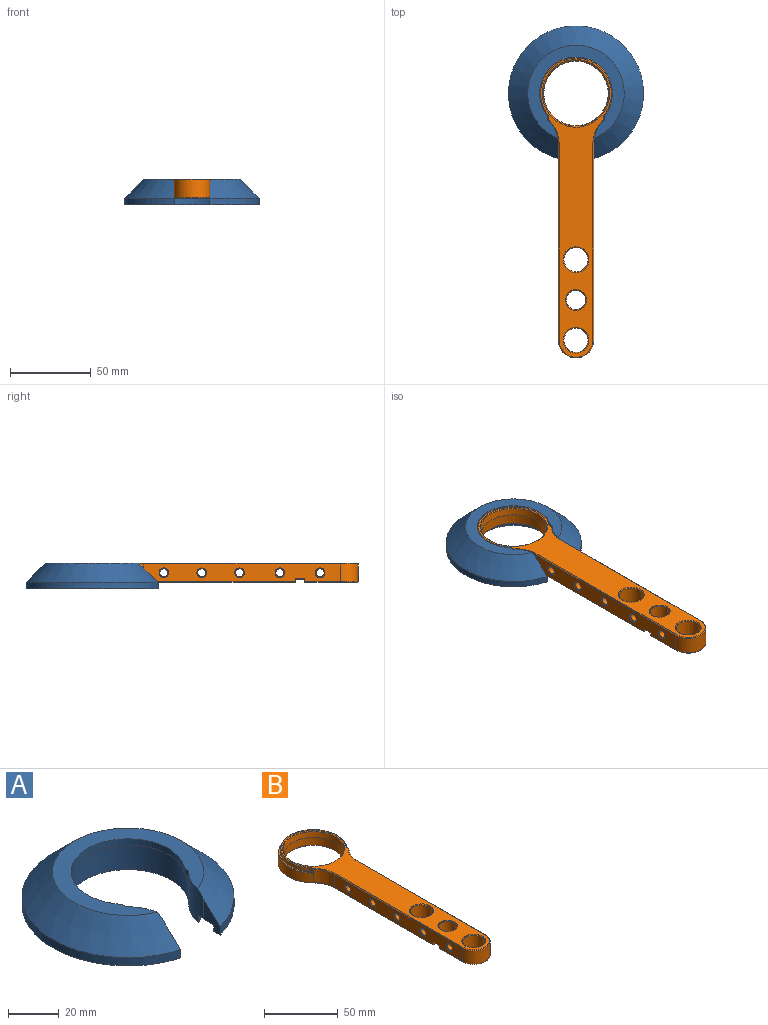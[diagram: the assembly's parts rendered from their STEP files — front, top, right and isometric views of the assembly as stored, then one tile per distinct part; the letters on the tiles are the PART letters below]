
ASSEMBLY  parts=2 mates=1
PART A: 75 faces, bbox 84.2x82.8x16.3 mm
  f0: cylinder r=19.95mm len=16mm, axis (0,0,-1), area 229.2mm2, adj f2,f36,f42,f43,f46,f51,f52,f72
  f1: cylinder r=19.95mm len=16mm, axis (0,0,-1), area 229.2mm2, adj f2,f35,f42,f43,f47,f51,f53,f69
  f2: plane 58.74x53.48mm, normal (0,0,-1), area 238.1mm2, adj f0,f1,f3,f4,f5,f6,f7,f8
  f3: cylinder r=18.5mm len=14.5mm, axis (0,0,-1), area 189mm2, adj f2,f38,f39,f49,f50,f72,f74
  f4: cylinder r=18.5mm len=14.5mm, axis (0,0,-1), area 189mm2, adj f2,f24,f25,f26,f48,f69,f70
  f5: plane 14.99x14.54mm, normal (1,0,0), area 129.4mm2, adj f2,f15,f16,f17,f18,f45,f66,f67
  f6: plane 14.99x14.54mm, normal (-1,0,0), area 129.4mm2, adj f2,f31,f32,f33,f34,f45,f66,f67
  f7: plane 14.54x12.99mm, normal (0.5,0.87,0), area 129.4mm2, adj f2,f31,f32,f33,f34,f45,f63,f64
  f8: plane 14.54x12.99mm, normal (-0.5,-0.87,0), area 129.4mm2, adj f2,f27,f28,f29,f30,f45,f63,f64
  f9: plane 14.54x12.99mm, normal (-0.5,0.87,0), area 129.4mm2, adj f2,f27,f28,f29,f30,f45,f60,f61
  f10: plane 14.54x12.99mm, normal (0.5,-0.87,0), area 129.4mm2, adj f2,f23,f24,f25,f26,f45,f60,f61
  f11: plane 14.54x12.99mm, normal (-0.5,-0.87,0), area 129.4mm2, adj f2,f37,f38,f39,f45,f50,f57,f58
  f12: plane 14.54x12.99mm, normal (0.5,0.87,0), area 129.4mm2, adj f2,f19,f20,f21,f22,f45,f57,f58
  f13: plane 14.54x12.99mm, normal (0.5,-0.87,0), area 129.4mm2, adj f2,f19,f20,f21,f22,f45,f54,f55
  f14: plane 14.54x12.99mm, normal (-0.5,0.87,0), area 129.4mm2, adj f2,f15,f16,f17,f18,f45,f54,f55
  f15: cylinder r=40.45mm len=33.9mm, axis (0,0,-1), area 138mm2, adj f5,f14,f16,f45
  f16: cone r=40.45mm half-angle=45deg, axis (0,0,-1), area 550.6mm2, adj f5,f14,f15,f17
  f17: plane 24.27x15.93mm, normal (0,0,-1), area 104.2mm2, adj f5,f14,f16,f18
  f18: cylinder r=25.5mm len=20.95mm, axis (0,0,-1), area 365.4mm2, adj f2,f5,f14,f17
  f19: cylinder r=40.45mm len=39.14mm, axis (0,0,-1), area 138mm2, adj f12,f13,f20,f45
  f20: cone r=40.45mm half-angle=45deg, axis (0,0,-1), area 550.6mm2, adj f12,f13,f19,f21
  f21: plane 28.02x6.88mm, normal (0,0,-1), area 104.2mm2, adj f12,f13,f20,f22
  f22: cylinder r=25.5mm len=24.19mm, axis (0,0,-1), area 365.4mm2, adj f2,f12,f13,f21
  f23: cylinder r=40.45mm len=22.15mm, axis (0,0,-1), area 97.6mm2, adj f10,f24,f45,f48
  f24: cone r=40.45mm half-angle=45deg, axis (0,0,-1), area 357.9mm2, adj f4,f10,f23,f25,f48
  f25: plane 12.8x11.82mm, normal (0,0,-1), area 48.4mm2, adj f4,f10,f24,f26
  f26: cylinder r=25.5mm len=14.5mm, axis (0,0,-1), area 87.3mm2, adj f2,f4,f10,f25
  f27: cylinder r=40.45mm len=39.14mm, axis (0,0,-1), area 138mm2, adj f8,f9,f28,f45
  f28: cone r=40.45mm half-angle=45deg, axis (0,0,-1), area 550.6mm2, adj f8,f9,f27,f29
  f29: plane 28.02x6.88mm, normal (0,0,-1), area 104.2mm2, adj f8,f9,f28,f30
  f30: cylinder r=25.5mm len=24.19mm, axis (0,0,-1), area 365.4mm2, adj f2,f8,f9,f29
  f31: cylinder r=40.45mm len=33.9mm, axis (0,0,-1), area 138mm2, adj f6,f7,f32,f45
  f32: cone r=40.45mm half-angle=45deg, axis (0,0,-1), area 550.6mm2, adj f6,f7,f31,f33
  f33: plane 24.27x15.93mm, normal (0,0,-1), area 104.2mm2, adj f6,f7,f32,f34
  f34: cylinder r=25.5mm len=20.95mm, axis (0,0,-1), area 365.4mm2, adj f2,f6,f7,f33
  f35: cylinder r=3.95mm len=3.19mm, axis (0,0,-1), area 10.1mm2, adj f1,f40,f41,f42
  f36: cylinder r=3.95mm len=3.19mm, axis (0,0,-1), area 10.1mm2, adj f0,f40,f41,f42
  f37: cylinder r=40.45mm len=22.15mm, axis (0,0,-1), area 97.6mm2, adj f11,f38,f45,f49
  f38: cone r=40.45mm half-angle=45deg, axis (0,0,-1), area 357.9mm2, adj f3,f11,f37,f39,f49
  f39: plane 12.8x11.82mm, normal (0,0,-1), area 48.4mm2, adj f3,f11,f38,f50
  f40: plane 48.15x40.62mm, normal (0,0,-1), area 163.2mm2, adj f35,f36,f41,f51
  f41: cylinder r=22.55mm len=45.1mm, axis (0,0,-1), area 298.3mm2, adj f35,f36,f40,f42
  f42: plane 59.9x57.66mm, normal (0,0,1), area 1003.5mm2, adj f0,f1,f35,f36,f41,f43
  f43: cone r=41.95mm half-angle=45deg, axis (0,0,-1), area 3447.3mm2, adj f0,f1,f42,f44,f46,f47
  f44: cylinder r=41.95mm len=83.9mm, axis (0,0,-1), area 964.9mm2, adj f43,f45,f46,f47
  f45: plane 83.9x82.42mm, normal (0,0,-1), area 375.8mm2, adj f5,f6,f7,f8,f9,f10,f11,f12
  f46: plane 13.16x9.58mm, normal (-1,0,0), area 60mm2, adj f0,f43,f44,f45,f73,f74
  f47: plane 13.16x9.58mm, normal (1,0,0), area 60mm2, adj f1,f43,f44,f45,f69,f71
  f48: plane 10.43x7.48mm, normal (-1,0,0), area 32.8mm2, adj f4,f23,f24,f45,f69,f71
  f49: plane 10.43x7.48mm, normal (1,0,0), area 32.8mm2, adj f3,f37,f38,f45,f73,f74
  f50: cylinder r=25.5mm len=14.5mm, axis (0,0,-1), area 87.3mm2, adj f2,f3,f11,f39
  f51: cylinder r=24.08mm len=48.15mm, axis (0,0,-1), area 1497mm2, adj f0,f1,f2,f40,f52,f53
  f52: plane 1.08x1.07mm, normal (0,0,-1), area 0mm2, adj f0,f51
  f53: plane 1.08x1.07mm, normal (0,0,-1), area 0mm2, adj f1,f51
  f54: plane 7.68x5.3mm, normal (0,0,-1), area 12mm2, adj f13,f14,f55,f56
  f55: cylinder r=38.45mm len=3.2mm, axis (0,0,-1), area 4.8mm2, adj f13,f14,f45,f54
  f56: cylinder r=30.45mm len=3.2mm, axis (0,0,-1), area 4.8mm2, adj f2,f13,f14,f54
  f57: plane 7.68x5.3mm, normal (0,0,-1), area 12mm2, adj f11,f12,f58,f59
  f58: cylinder r=38.45mm len=3.2mm, axis (0,0,-1), area 4.8mm2, adj f11,f12,f45,f57
  f59: cylinder r=30.45mm len=3.2mm, axis (0,0,-1), area 4.8mm2, adj f2,f11,f12,f57
  f60: plane 7.68x5.3mm, normal (0,0,-1), area 12mm2, adj f9,f10,f61,f62
  f61: cylinder r=38.45mm len=3.2mm, axis (0,0,-1), area 4.8mm2, adj f9,f10,f45,f60
  f62: cylinder r=30.45mm len=3.2mm, axis (0,0,-1), area 4.8mm2, adj f2,f9,f10,f60
  f63: plane 7.68x5.3mm, normal (0,0,-1), area 12mm2, adj f7,f8,f64,f65
  f64: cylinder r=38.45mm len=3.2mm, axis (0,0,-1), area 4.8mm2, adj f7,f8,f45,f63
  f65: cylinder r=30.45mm len=3.2mm, axis (0,0,-1), area 4.8mm2, adj f2,f7,f8,f63
  f66: plane 8.01x1.5mm, normal (0,0,-1), area 12mm2, adj f5,f6,f67,f68
  f67: cylinder r=38.45mm len=3.2mm, axis (0,0,-1), area 4.8mm2, adj f5,f6,f45,f66
  f68: cylinder r=30.45mm len=3.2mm, axis (0,0,-1), area 4.8mm2, adj f2,f5,f6,f66
  f69: plane 9.23x1.81mm, normal (0,0,-1), area 12.6mm2, adj f1,f4,f47,f48,f70,f71
  f70: cylinder r=30.45mm len=3.2mm, axis (0,0,-1), area 5.5mm2, adj f1,f2,f4,f69
  f71: cylinder r=38.45mm len=3.2mm, axis (0,0,-1), area 4.9mm2, adj f45,f47,f48,f69
  f72: cylinder r=30.45mm len=3.2mm, axis (0,0,-1), area 5.5mm2, adj f0,f2,f3,f74
  f73: cylinder r=38.45mm len=3.2mm, axis (0,0,-1), area 4.9mm2, adj f45,f46,f49,f74
  f74: plane 9.23x1.81mm, normal (0,0,-1), area 12.6mm2, adj f0,f3,f46,f49,f72,f73
PART B: 91 faces, bbox 48x188.2x12 mm
  f0: cylinder r=24mm len=48mm, axis (0,0,-1), area 910.7mm2, adj f5,f11,f26,f27,f35,f42,f43,f62
  f1: plane 185.73x44mm, normal (0,0,1), area 2605.8mm2, adj f33,f34,f35,f36,f37,f38,f39,f40
  f2: plane 148.73x47mm, normal (0,0,-1), area 2328.4mm2, adj f54,f55,f58,f59,f62,f63,f65,f66
  f3: cylinder r=8mm len=14.29mm, axis (0,0,-1), area 26.5mm2, adj f15,f31,f32,f52
  f4: cylinder r=6mm len=12mm, axis (0,0,-1), area 320.4mm2, adj f44,f90
  f5: cylinder r=20mm len=14.19mm, axis (0,0,-1), area 173.6mm2, adj f0,f6,f33,f58
  f6: plane 122x11mm, normal (-1,0,0), area 1188.6mm2, adj f5,f7,f34,f45,f47,f48,f53,f54
  f7: cylinder r=11mm len=22mm, axis (0,0,-1), area 380.1mm2, adj f6,f8,f36,f57
  f8: plane 122x11mm, normal (1,0,0), area 1188.6mm2, adj f7,f11,f38,f61,f67,f68,f70,f72
  f9: cylinder r=7.5mm len=15mm, axis (0,0,-1), area 518.4mm2, adj f74,f85
  f10: cylinder r=7.5mm len=15mm, axis (0,0,-1), area 518.4mm2, adj f73,f87
  f11: cylinder r=20mm len=14.19mm, axis (0,0,-1), area 173.6mm2, adj f0,f8,f40,f65
  f12: cylinder r=20mm len=40mm, axis (0,0,-1), area 816.8mm2, adj f86,f88
  f13: plane 32.5x21mm, normal (0,0,-1), area 370.2mm2, adj f46,f49,f52,f53,f56,f57,f60,f61
  f14: cylinder r=8mm len=14.29mm, axis (0,0,-1), area 26.5mm2, adj f15,f29,f30,f63
  f15: plane 21x16mm, normal (0,0,-1), area 74.6mm2, adj f3,f14,f21,f22,f23,f24,f29,f30
  f16: cylinder r=2.5mm len=21mm, axis (1,0,0), area 329.9mm2, adj f75,f76
  f17: cylinder r=2.5mm len=21mm, axis (1,0,0), area 329.9mm2, adj f77,f78
  f18: cylinder r=2.5mm len=21mm, axis (1,0,0), area 329.9mm2, adj f79,f80
  f19: cylinder r=2.5mm len=21mm, axis (1,0,0), area 329.9mm2, adj f81,f82
  f20: cylinder r=2.5mm len=21mm, axis (1,0,0), area 329.9mm2, adj f83,f84
  f21: plane 1.57x1.5mm, normal (0,-1,0), area 2.4mm2, adj f15,f30,f48,f55
  f22: plane 1.57x1.5mm, normal (0,1,0), area 2.4mm2, adj f15,f32,f46,f47
  f23: plane 1.57x1.5mm, normal (0,-1,0), area 2.4mm2, adj f15,f29,f69,f72
  f24: plane 1.57x1.5mm, normal (0,1,0), area 2.4mm2, adj f15,f31,f60,f67
  f25: plane 47x39.35mm, normal (0,0,1), area 104.8mm2, adj f26,f27,f28,f43
  f26: cylinder r=4mm len=3.17mm, axis (0,0,1), area 8.5mm2, adj f0,f25,f28,f37,f43
  f27: cylinder r=4mm len=3.17mm, axis (0,0,1), area 8.5mm2, adj f0,f25,f28,f41,f43
  f28: cylinder r=22.5mm len=45mm, axis (0,0,1), area 248mm2, adj f25,f26,f27,f39
  f29: cylinder r=2mm len=1.79mm, axis (0,0,-1), area 3.3mm2, adj f14,f15,f23,f66
  f30: cylinder r=2mm len=1.79mm, axis (0,0,-1), area 3.3mm2, adj f14,f15,f21,f59
  f31: cylinder r=2mm len=1.79mm, axis (0,0,-1), area 3.3mm2, adj f3,f15,f24,f56
  f32: cylinder r=2mm len=1.79mm, axis (0,0,-1), area 3.3mm2, adj f3,f15,f22,f49
  f33: cone r=20mm half-angle=45deg, axis (0,0,1), area 11.3mm2, adj f1,f5,f34,f35
  f34: plane 122x0.5mm, normal (-0.71,0,0.71), area 86.3mm2, adj f1,f6,f33,f36
  f35: cone r=23.5mm half-angle=45deg, axis (0,0,-1), area 0.4mm2, adj f0,f1,f33,f37
  f36: cone r=10.5mm half-angle=45deg, axis (0,0,-1), area 23.9mm2, adj f1,f7,f34,f38
  f37: cone r=4.5mm half-angle=45deg, axis (0,0,1), area 2.4mm2, adj f1,f26,f35,f39
  f38: plane 122x0.5mm, normal (0.71,0,0.71), area 86.3mm2, adj f1,f8,f36,f40
  f39: cone r=22mm half-angle=45deg, axis (0,0,-1), area 69.4mm2, adj f1,f28,f37,f41
  f40: cone r=20mm half-angle=45deg, axis (0,0,1), area 11.3mm2, adj f1,f11,f38,f42
  f41: cone r=4mm half-angle=45deg, axis (0,0,1), area 2.4mm2, adj f1,f27,f39,f42
  f42: cone r=23.5mm half-angle=45deg, axis (0,0,-1), area 0.4mm2, adj f0,f1,f40,f41
  f43: cone r=23.5mm half-angle=45deg, axis (0,0,-1), area 77.9mm2, adj f0,f25,f26,f27
  f44: cone r=6mm half-angle=45deg, axis (0,0,1), area 27.8mm2, adj f1,f4
  f45: plane 6x0.5mm, normal (-0.71,0,-0.71), area 3.9mm2, adj f6,f15,f47,f48
  f46: plane 1.57x0.5mm, normal (0,0.71,-0.71), area 1.1mm2, adj f13,f22,f49,f50
  f47: plane 2x0.5mm, normal (-0.71,0.71,0), area 1.2mm2, adj f6,f22,f45,f50
  f48: plane 2x0.5mm, normal (-0.71,-0.71,0), area 1.2mm2, adj f6,f21,f45,f51
  f49: cone r=1.5mm half-angle=45deg, axis (0,0,1), area 1.4mm2, adj f13,f32,f46,f52
  f50: plane 0.5x0.5mm, normal (-0.58,0.58,-0.58), area 0.2mm2, adj f46,f47,f53
  f51: plane 0.5x0.5mm, normal (-0.58,-0.58,-0.58), area 0.2mm2, adj f48,f54,f55
  f52: cone r=8mm half-angle=45deg, axis (0,0,-1), area 12.9mm2, adj f3,f13,f49,f56
  f53: plane 22x0.5mm, normal (-0.71,0,-0.71), area 15.6mm2, adj f6,f13,f50,f57
  f54: plane 94x0.5mm, normal (-0.71,0,-0.71), area 66.5mm2, adj f2,f6,f51,f58
  f55: plane 1.57x0.5mm, normal (0,-0.71,-0.71), area 1.1mm2, adj f2,f21,f51,f59
  f56: cone r=1.5mm half-angle=45deg, axis (0,0,1), area 1.4mm2, adj f13,f31,f52,f60
  f57: cone r=11mm half-angle=45deg, axis (0,0,1), area 23.9mm2, adj f7,f13,f53,f61
  f58: cone r=20.5mm half-angle=45deg, axis (0,0,-1), area 11.3mm2, adj f2,f5,f54,f62
  f59: cone r=1.5mm half-angle=45deg, axis (0,0,1), area 1.4mm2, adj f2,f30,f55,f63
  f60: plane 1.57x0.5mm, normal (0,0.71,-0.71), area 1.1mm2, adj f13,f24,f56,f64
  f61: plane 22x0.5mm, normal (0.71,0,-0.71), area 15.6mm2, adj f8,f13,f57,f64
  f62: cone r=24mm half-angle=45deg, axis (0,0,1), area 79.3mm2, adj f0,f2,f58,f65
  f63: cone r=8mm half-angle=45deg, axis (0,0,-1), area 12.9mm2, adj f2,f14,f59,f66
  f64: plane 0.5x0.5mm, normal (0.58,0.58,-0.58), area 0.2mm2, adj f60,f61,f67
  f65: cone r=20.5mm half-angle=45deg, axis (0,0,-1), area 11.3mm2, adj f2,f11,f62,f68
  f66: cone r=1.5mm half-angle=45deg, axis (0,0,1), area 1.4mm2, adj f2,f29,f63,f69
  f67: plane 2x0.5mm, normal (0.71,0.71,0), area 1.2mm2, adj f8,f24,f64,f70
  f68: plane 94x0.5mm, normal (0.71,0,-0.71), area 66.5mm2, adj f2,f8,f65,f71
  f69: plane 1.57x0.5mm, normal (0,-0.71,-0.71), area 1.1mm2, adj f2,f23,f66,f71
  f70: plane 6x0.5mm, normal (0.71,0,-0.71), area 3.9mm2, adj f8,f15,f67,f72
  f71: plane 0.5x0.5mm, normal (0.58,-0.58,-0.58), area 0.2mm2, adj f68,f69,f72
  f72: plane 2x0.5mm, normal (0.71,-0.71,0), area 1.2mm2, adj f8,f23,f70,f71
  f73: cone r=7.5mm half-angle=45deg, axis (0,0,1), area 34.4mm2, adj f1,f10
  f74: cone r=7.5mm half-angle=45deg, axis (0,0,1), area 34.4mm2, adj f1,f9
  f75: cone r=2.5mm half-angle=45deg, axis (-1,0,0), area 12.2mm2, adj f6,f16
  f76: cone r=2.5mm half-angle=45deg, axis (1,0,0), area 12.2mm2, adj f8,f16
  f77: cone r=2.5mm half-angle=45deg, axis (-1,0,0), area 12.2mm2, adj f6,f17
  f78: cone r=2.5mm half-angle=45deg, axis (1,0,0), area 12.2mm2, adj f8,f17
  f79: cone r=2.5mm half-angle=45deg, axis (-1,0,0), area 12.2mm2, adj f6,f18
  f80: cone r=2.5mm half-angle=45deg, axis (1,0,0), area 12.2mm2, adj f8,f18
  f81: cone r=2.5mm half-angle=45deg, axis (-1,0,0), area 12.2mm2, adj f6,f19
  f82: cone r=2.5mm half-angle=45deg, axis (1,0,0), area 12.2mm2, adj f8,f19
  f83: cone r=2.5mm half-angle=45deg, axis (-1,0,0), area 12.2mm2, adj f6,f20
  f84: cone r=2.5mm half-angle=45deg, axis (1,0,0), area 12.2mm2, adj f8,f20
  f85: cone r=8mm half-angle=45deg, axis (0,0,-1), area 34.4mm2, adj f2,f9
  f86: cone r=20.5mm half-angle=45deg, axis (0,0,-1), area 90mm2, adj f2,f12
  f87: cone r=8mm half-angle=45deg, axis (0,0,-1), area 34.4mm2, adj f10,f13
  f88: cone r=20mm half-angle=5deg, axis (0,0,1), area 573.5mm2, adj f12,f89
  f89: cone r=20.94mm half-angle=47.5deg, axis (0,0,1), area 95.7mm2, adj f1,f88
  f90: cone r=6mm half-angle=45deg, axis (0,0,-1), area 57.8mm2, adj f4,f15
PLACE A at identity
PLACE B t=(0,0,-12)mm
MATE fastened A.f15 <-> B.f12  axis (0,0,1) through (0,0,0)mm
